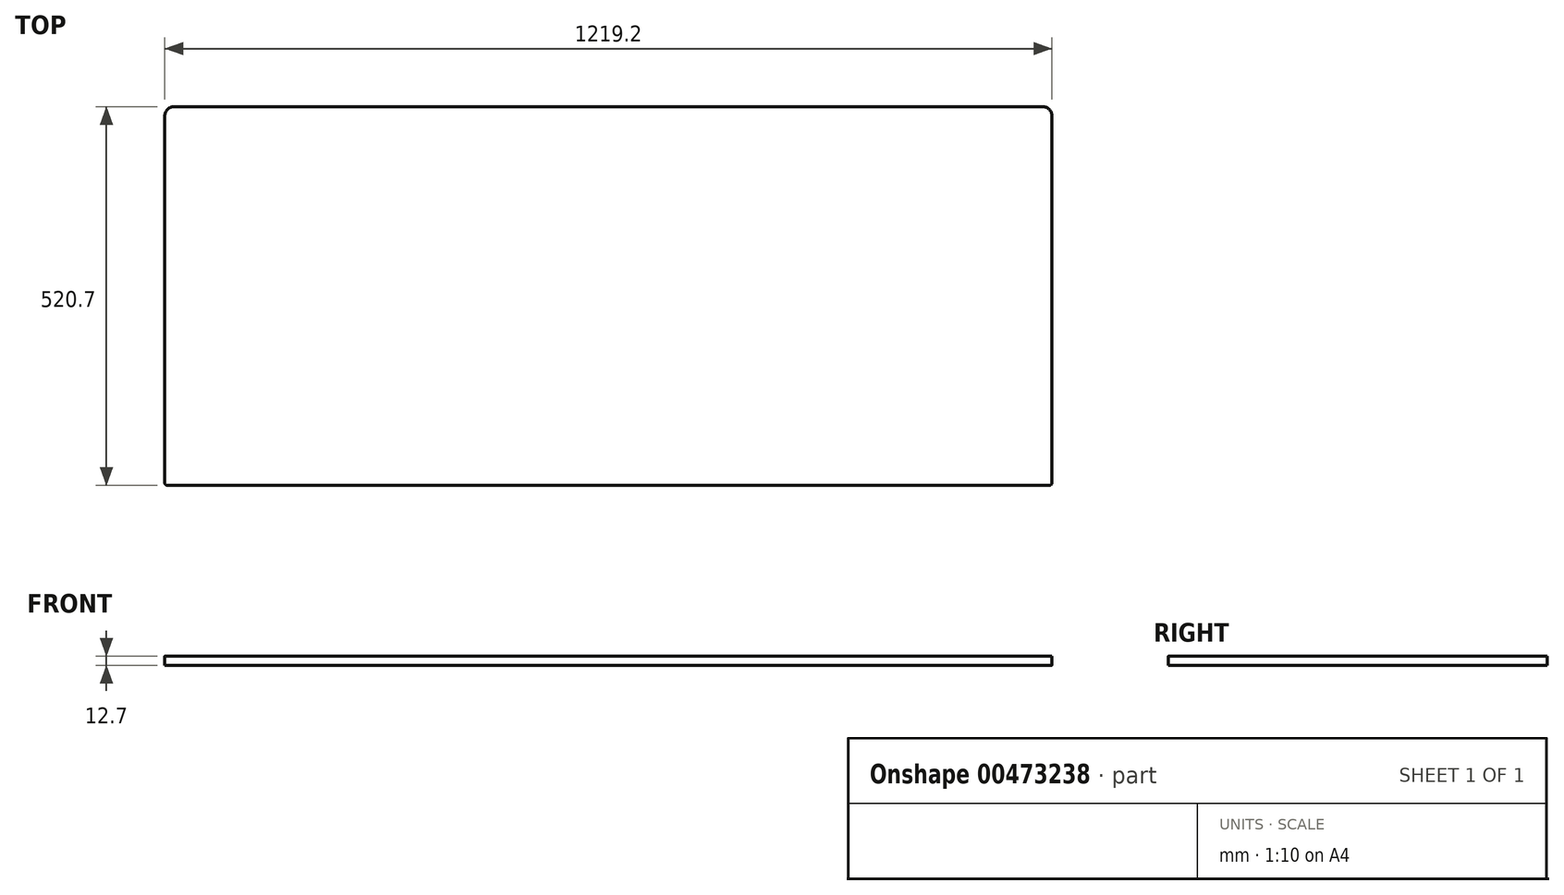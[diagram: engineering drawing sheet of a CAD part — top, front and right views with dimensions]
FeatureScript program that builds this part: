
annotation { "Feature Type Name" : "Feature", "Feature Type Description" : "" }
export const myFeature = defineFeature(function(context is Context, id is Id, definition is map)
    precondition{}
    {
        {
            var Q0;
            Q0=qCreatedBy(makeId("Top.planeOp"),FACE);
            var sketch = newSketch(context, id + "F0", { "sketchPlane" : qUnion([Q0])});
            skLineSegment(sketch, "E0.bottom", {"start": v(609.6, 260.35) * mm, "end": v(-609.6, 260.35) * mm});
            skLineSegment(sketch, "E0.top", {"start": v(609.6, -260.35) * mm, "end": v(-609.6, -260.35) * mm});
            skLineSegment(sketch, "E0.left", {"start": v(609.6, 260.35) * mm, "end": v(609.6, -260.35) * mm});
            skLineSegment(sketch, "E0.right", {"start": v(-609.6, 260.35) * mm, "end": v(-609.6, -260.35) * mm});
            skPoint(sketch, "E0.middle", {"position": v(0, 0) * mm});
            skSolve(sketch);
        }
        {
            var Q0;
            Q0=makeQuery(id+"F0.imprint","IMPRINT",FACE,{"disambiguationData":[TD([[makeQuery(id+"F0.imprint","IMPRINT",EDGE,{"derivedFrom":sQuery(id+"F0.wireOp",EDGE,"E0.bottom")}),1.0]])]});
            extrude(context, id + "F1", {"entities" : qUnion([Q0]), "oppositeDirection" : true, "depth" : 12.7 * mm});
        }
        {
            var Q0;
            Q0=makeQuery(id+"F1.opExtrude","SWEPT_EDGE",EDGE,{"disambiguationData":[OSD([sQuery(id+"F0.wireOp",EDGE,"E0.top"),sQuery(id+"F0.wireOp",EDGE,"E0.left")])]});
            var Q1;
            Q1=makeQuery(id+"F1.opExtrude","SWEPT_EDGE",EDGE,{"disambiguationData":[OSD([sQuery(id+"F0.wireOp",EDGE,"E0.top"),sQuery(id+"F0.wireOp",EDGE,"E0.right")])]});
            fillet(context, id + "F2", {"entities" : qUnion([Q0, Q1]), "radius" : 3.17 * mm, "tangentPropagation" : true, "allowEdgeOverflow" : false});
        }
        {
            var Q0;
            Q0=makeQuery(id+"F1.opExtrude","SWEPT_EDGE",EDGE,{"disambiguationData":[OSD([sQuery(id+"F0.wireOp",EDGE,"E0.bottom"),sQuery(id+"F0.wireOp",EDGE,"E0.left")])]});
            var Q1;
            Q1=makeQuery(id+"F1.opExtrude","SWEPT_EDGE",EDGE,{"disambiguationData":[OSD([sQuery(id+"F0.wireOp",EDGE,"E0.bottom"),sQuery(id+"F0.wireOp",EDGE,"E0.right")])]});
            fillet(context, id + "F3", {"entities" : qUnion([Q0, Q1]), "radius" : 12.7 * mm, "tangentPropagation" : true, "allowEdgeOverflow" : false});
        }
    });
